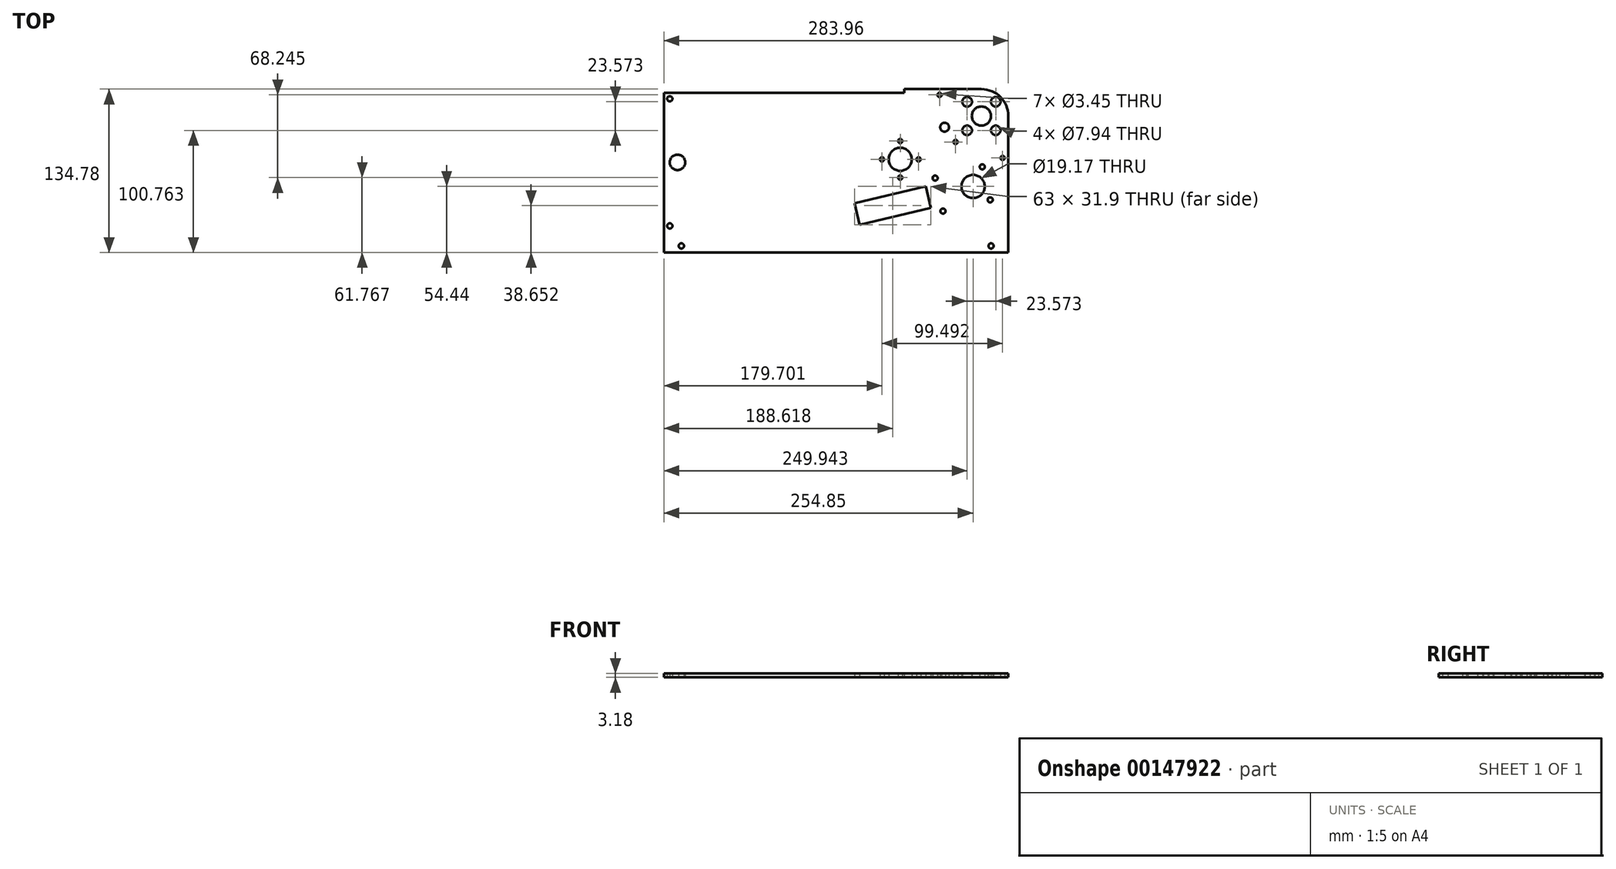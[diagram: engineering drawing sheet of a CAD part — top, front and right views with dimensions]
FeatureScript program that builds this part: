
annotation { "Feature Type Name" : "Feature", "Feature Type Description" : "" }
export const myFeature = defineFeature(function(context is Context, id is Id, definition is map)
    precondition{}
    {
        {
            var Q0;
            Q0=qCreatedBy(makeId("Top.planeOp"),FACE);
            var sketch = newSketch(context, id + "F0", { "sketchPlane" : qUnion([Q0])});
            skCircle(sketch, "E0", {"center": v(0, 0) * mm, "radius": 7.94 * mm});
            skLineSegment(sketch, "E1.bottom", {"start": v(-63.67, 22.23) * mm, "end": v(0, 22.23) * mm});
            skLineSegment(sketch, "E1.top", {"start": v(-261.73, -112.55) * mm, "end": v(22.23, -112.55) * mm});
            skLineSegment(sketch, "E1.left", {"start": v(-261.73, 19.05) * mm, "end": v(-261.73, -112.55) * mm});
            skArc(sketch, "E2", {"start": v(22.23, 0) * mm, "mid": v(15.72, 15.72) * mm, "end": v(0, 22.23) * mm});
            skLineSegment(sketch, "E3", {"start": v(22.23, -112.55) * mm, "end": v(22.23, -101.75) * mm});
            skLineSegment(sketch, "E4", {"start": v(22.23, -101.75) * mm, "end": v(22.23, 0) * mm});
            skLineSegment(sketch, "E5", {"start": v(0, 0) * mm, "end": v(0, -112.55) * mm, "construction": true});
            skLineSegment(sketch, "E6", {"start": v(22.23, -107.15) * mm, "end": v(7.94, -107.15) * mm, "construction": true});
            skCircle(sketch, "E7", {"center": v(7.94, -107.15) * mm, "radius": 2.15 * mm});
            skLineSegment(sketch, "E8", {"start": v(-261.73, -107.15) * mm, "end": v(-247.45, -107.15) * mm, "construction": true});
            skCircle(sketch, "E9", {"center": v(-247.45, -107.15) * mm, "radius": 2.15 * mm});
            skCircle(sketch, "E10", {"center": v(-256.97, 14.29) * mm, "radius": 2.15 * mm});
            skLineSegment(sketch, "E11", {"start": v(-256.97, 14.29) * mm, "end": v(-256.97, -90.64) * mm, "construction": true});
            skLineSegment(sketch, "E12", {"start": v(-256.97, -90.64) * mm, "end": v(-256.97, -107.15) * mm, "construction": true});
            skCircle(sketch, "E13", {"center": v(-256.97, -90.64) * mm, "radius": 2.15 * mm});
            skLineSegment(sketch, "E14.bottom", {"start": v(-38.19, -51.18) * mm, "end": v(0.72, -41.9) * mm, "construction": true});
            skLineSegment(sketch, "E14.top", {"start": v(-31.7, -78.42) * mm, "end": v(7.21, -69.14) * mm, "construction": true});
            skLineSegment(sketch, "E14.left", {"start": v(-38.19, -51.18) * mm, "end": v(-31.7, -78.42) * mm, "construction": true});
            skLineSegment(sketch, "E14.right", {"start": v(0.72, -41.9) * mm, "end": v(7.21, -69.14) * mm, "construction": true});
            skCircle(sketch, "E15", {"center": v(-6.88, -58.11) * mm, "radius": 9.59 * mm});
            skCircle(sketch, "E16", {"center": v(-38.19, -51.18) * mm, "radius": 2.1 * mm});
            skCircle(sketch, "E17", {"center": v(-31.7, -78.42) * mm, "radius": 2.1 * mm});
            skCircle(sketch, "E18", {"center": v(7.21, -69.14) * mm, "radius": 2.1 * mm});
            skCircle(sketch, "E19", {"center": v(0.72, -41.9) * mm, "radius": 2.1 * mm});
            skLineSegment(sketch, "E20", {"start": v(0, 0) * mm, "end": v(-6.88, -58.11) * mm, "construction": true});
            skLineSegment(sketch, "E21", {"start": v(0, 0) * mm, "end": v(17.46, -34.55) * mm, "construction": true});
            skLineSegment(sketch, "E22", {"start": v(0, 0) * mm, "end": v(-34.55, 17.46) * mm, "construction": true});
            skLineSegment(sketch, "E23", {"start": v(0, 0) * mm, "end": v(-21.33, -21.33) * mm, "construction": true});
            skLineSegment(sketch, "E24", {"start": v(-21.33, -21.33) * mm, "end": v(17.46, -34.55) * mm, "construction": true});
            skLineSegment(sketch, "E25", {"start": v(-21.33, -21.33) * mm, "end": v(-34.55, 17.46) * mm, "construction": true});
            skCircle(sketch, "E26", {"center": v(-34.55, 17.46) * mm, "radius": 4.76 * mm, "construction": true});
            skCircle(sketch, "E27", {"center": v(-34.55, 17.46) * mm, "radius": 1.73 * mm});
            skCircle(sketch, "E28", {"center": v(-21.33, -21.33) * mm, "radius": 1.73 * mm});
            skCircle(sketch, "E29", {"center": v(17.46, -34.55) * mm, "radius": 1.73 * mm});
            skLineSegment(sketch, "E30", {"start": v(-256.97, 14.29) * mm, "end": v(-256.97, 19.05) * mm, "construction": true});
            skLineSegment(sketch, "E31", {"start": v(-256.97, 14.29) * mm, "end": v(-261.73, 14.29) * mm, "construction": true});
            skCircle(sketch, "E32", {"center": v(17.46, -34.55) * mm, "radius": 4.76 * mm, "construction": true});
            skLineSegment(sketch, "E33", {"start": v(-1.93, -27.94) * mm, "end": v(-3.47, -32.45) * mm, "construction": true});
            skLineSegment(sketch, "E34", {"start": v(15.93, -39.06) * mm, "end": v(-3.47, -32.45) * mm, "construction": true});
            skLineSegment(sketch, "E35", {"start": v(-34.94, -64.8) * mm, "end": v(-43.75, -66.9) * mm, "construction": true});
            skLineSegment(sketch, "E36.bottom", {"start": v(-45.88, -57.95) * mm, "end": v(-104.61, -71.95) * mm});
            skLineSegment(sketch, "E36.top", {"start": v(-41.61, -75.85) * mm, "end": v(-100.34, -89.85) * mm});
            skLineSegment(sketch, "E36.left", {"start": v(-45.88, -57.95) * mm, "end": v(-41.61, -75.85) * mm});
            skLineSegment(sketch, "E36.right", {"start": v(-104.61, -71.95) * mm, "end": v(-100.34, -89.85) * mm});
            skLineSegment(sketch, "E37", {"start": v(0, 0) * mm, "end": v(-30.36, -9.16) * mm, "construction": true});
            skCircle(sketch, "E38", {"center": v(-30.36, -9.16) * mm, "radius": 3.66 * mm});
            skLineSegment(sketch, "E39.bottom", {"start": v(11.79, 11.79) * mm, "end": v(-11.79, 11.79) * mm, "construction": true});
            skLineSegment(sketch, "E39.top", {"start": v(11.79, -11.79) * mm, "end": v(-11.79, -11.79) * mm, "construction": true});
            skLineSegment(sketch, "E39.left", {"start": v(11.79, 11.79) * mm, "end": v(11.79, -11.79) * mm, "construction": true});
            skLineSegment(sketch, "E39.right", {"start": v(-11.79, 11.79) * mm, "end": v(-11.79, -11.79) * mm, "construction": true});
            skCircle(sketch, "E40", {"center": v(-11.79, 11.79) * mm, "radius": 3.97 * mm});
            skCircle(sketch, "E41", {"center": v(11.79, 11.79) * mm, "radius": 3.97 * mm});
            skCircle(sketch, "E42", {"center": v(11.79, -11.79) * mm, "radius": 3.97 * mm});
            skCircle(sketch, "E43", {"center": v(-11.79, -11.79) * mm, "radius": 3.97 * mm});
            skLineSegment(sketch, "E44", {"start": v(-256.97, -38.18) * mm, "end": v(-250.62, -38.18) * mm, "construction": true});
            skCircle(sketch, "E45", {"center": v(-250.62, -38.18) * mm, "radius": 6.35 * mm});
            skLineSegment(sketch, "E46.top", {"start": v(-63.67, 19.05) * mm, "end": v(-261.73, 19.05) * mm});
            skLineSegment(sketch, "E46.left", {"start": v(-63.67, 22.22) * mm, "end": v(-63.67, 19.05) * mm});
            skLineSegment(sketch, "E47", {"start": v(-66.95, -112.55) * mm, "end": v(-66.95, -35.7) * mm, "construction": true});
            skLineSegment(sketch, "E48", {"start": v(22.23, -35.7) * mm, "end": v(-66.95, -35.7) * mm, "construction": true});
            skCircle(sketch, "E49", {"center": v(-66.95, -35.7) * mm, "radius": 11.11 * mm, "construction": true});
            skCircle(sketch, "E50", {"center": v(-66.95, -35.7) * mm, "radius": 9.53 * mm});
            skLineSegment(sketch, "E51.bottom", {"start": v(-66.95, -20.62) * mm, "end": v(-51.87, -35.7) * mm, "construction": true});
            skLineSegment(sketch, "E51.top", {"start": v(-82.03, -35.7) * mm, "end": v(-66.95, -50.78) * mm, "construction": true});
            skLineSegment(sketch, "E51.left", {"start": v(-66.95, -20.62) * mm, "end": v(-82.03, -35.7) * mm, "construction": true});
            skLineSegment(sketch, "E51.right", {"start": v(-51.87, -35.7) * mm, "end": v(-66.95, -50.78) * mm, "construction": true});
            skCircle(sketch, "E52", {"center": v(-66.95, -20.62) * mm, "radius": 3.97 * mm, "construction": true});
            skCircle(sketch, "E53", {"center": v(-66.95, -20.62) * mm, "radius": 1.73 * mm});
            skCircle(sketch, "E54", {"center": v(-51.87, -35.7) * mm, "radius": 1.73 * mm});
            skCircle(sketch, "E55", {"center": v(-66.95, -50.78) * mm, "radius": 1.73 * mm});
            skCircle(sketch, "E56", {"center": v(-82.03, -35.7) * mm, "radius": 1.73 * mm});
            skLineSegment(sketch, "E57", {"start": v(-6.88, -58.11) * mm, "end": v(3.97, -55.52) * mm, "construction": true});
            skCircle(sketch, "E58", {"center": v(-66.95, -50.78) * mm, "radius": 3.97 * mm, "construction": true});
            skLineSegment(sketch, "E59", {"start": v(-45.88, -57.95) * mm, "end": v(-47.7, -50.28) * mm, "construction": true});
            skLineSegment(sketch, "E60", {"start": v(-47.7, -50.28) * mm, "end": v(-66.03, -54.64) * mm, "construction": true});
            skSolve(sketch);
        }
        {
            var Q0;
            Q0=qSketchRegion(id+"F0",true);
            extrude(context, id + "F1", {"entities" : qUnion([Q0]), "depth" : 3.17 * mm});
        }
    });
